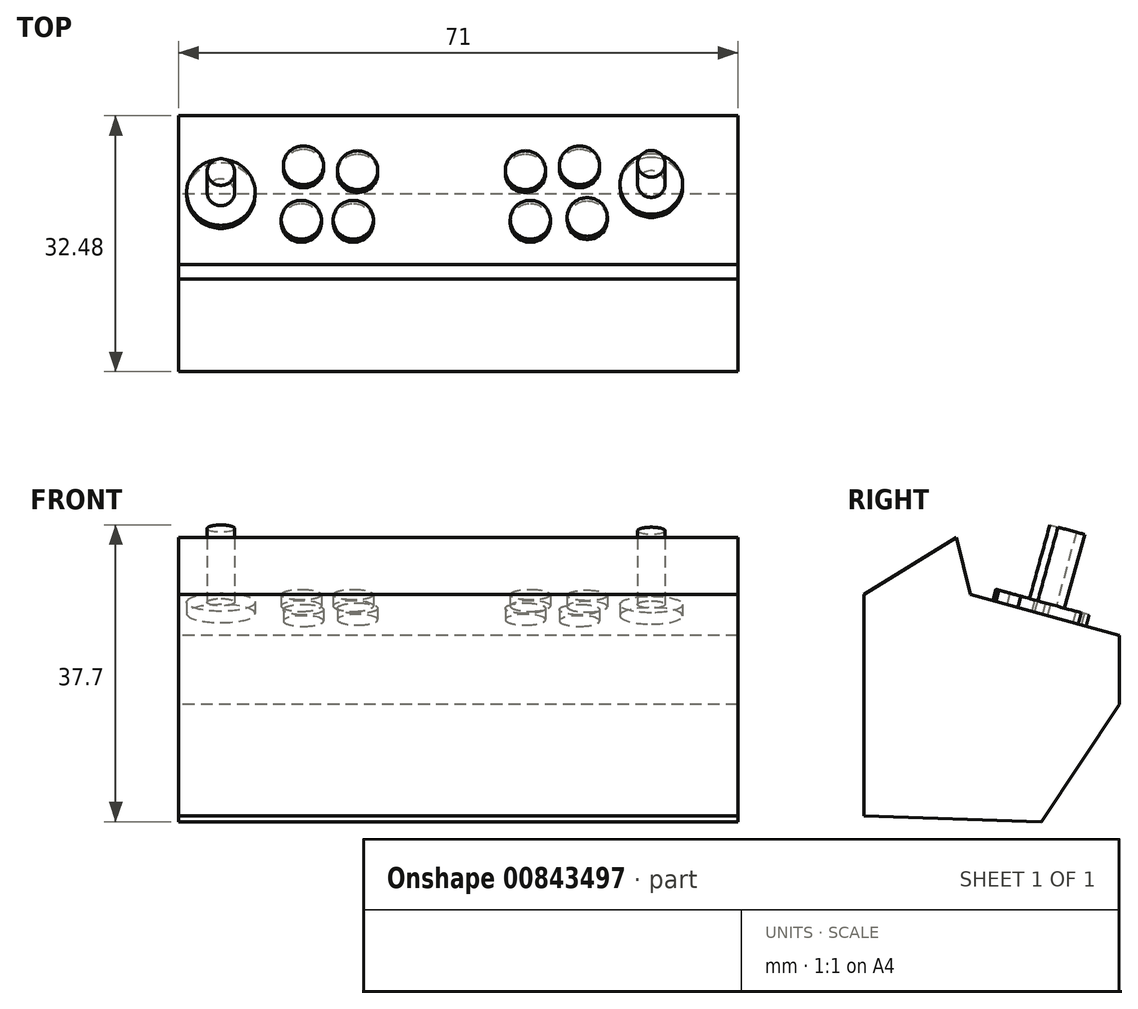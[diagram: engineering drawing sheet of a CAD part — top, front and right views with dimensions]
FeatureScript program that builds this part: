
annotation { "Feature Type Name" : "Feature", "Feature Type Description" : "" }
export const myFeature = defineFeature(function(context is Context, id is Id, definition is map)
    precondition{}
    {
        {
            var Q0;
            Q0=qCreatedBy(makeId("Right.planeOp"),FACE);
            var sketch = newSketch(context, id + "F0", { "sketchPlane" : qUnion([Q0])});
            skLineSegment(sketch, "E0", {"start": v(22.55, -11.2) * mm, "end": v(32.48, 3.7) * mm});
            skLineSegment(sketch, "E1", {"start": v(32.48, 3.7) * mm, "end": v(32.48, 12.46) * mm});
            skLineSegment(sketch, "E2", {"start": v(32.48, 12.46) * mm, "end": v(13.56, 17.66) * mm});
            skLineSegment(sketch, "E3", {"start": v(13.56, 17.66) * mm, "end": v(11.76, 24.88) * mm});
            skLineSegment(sketch, "E4", {"start": v(11.76, 24.88) * mm, "end": v(0, 17.66) * mm});
            skLineSegment(sketch, "E5", {"start": v(0, 17.66) * mm, "end": v(0, -10.48) * mm});
            skLineSegment(sketch, "E6", {"start": v(0, -10.48) * mm, "end": v(22.55, -11.2) * mm});
            skPoint(sketch, "E7.orphan", {"position": v(-45.1, 64.5) * mm});
            skPoint(sketch, "E8.start.orphan", {"position": v(-45.1, 37.53) * mm});
            skSolve(sketch);
        }
        {
            var Q0;
            Q0=makeQuery(id+"F0.imprint","IMPRINT",FACE,{"disambiguationData":[TD([[makeQuery(id+"F0.imprint","IMPRINT",EDGE,{"derivedFrom":sQuery(id+"F0.wireOp",EDGE,"E0")}),1.0]])]});
            extrude(context, id + "F1", {"entities" : qUnion([Q0]), "depth" : 65 * mm, "offsetDistance" : 25 * mm});
        }
        {
            var Q0;
            Q0=makeQuery(id+"F1.opExtrude","SWEPT_EDGE",EDGE,{"disambiguationData":[OSD([sQuery(id+"F0.wireOp",EDGE,"E0"),sQuery(id+"F0.wireOp",EDGE,"E1")])]});
            var Q1;
            Q1=makeQuery(id+"F1.opExtrude","SWEPT_EDGE",EDGE,{"disambiguationData":[OSD([sQuery(id+"F0.wireOp",EDGE,"E1"),sQuery(id+"F0.wireOp",EDGE,"E2")])]});
            fillet(context, id + "F2", {"entities" : qUnion([Q0, Q1]), "radius" : 2 * mm, "tangentPropagation" : true, "allowEdgeOverflow" : false});
        }
        {
            var Q0;
            Q0=makeQuery(id+"F1.opExtrude","SWEPT_FACE",FACE,{"disambiguationData":[OSD([sQuery(id+"F0.wireOp",EDGE,"E2")])]});
            var sketch = newSketch(context, id + "F3", { "sketchPlane" : qUnion([Q0])});
            skCircle(sketch, "E9", {"center": v(60.03, 18.6) * mm, "radius": 3.97 * mm});
            skCircle(sketch, "E10", {"center": v(5.35, 17.52) * mm, "radius": 4.35 * mm});
            skCircle(sketch, "E11", {"center": v(51.88, 14.27) * mm, "radius": 2.55 * mm});
            skCircle(sketch, "E12", {"center": v(50.9, 21.07) * mm, "radius": 2.55 * mm});
            skCircle(sketch, "E13", {"center": v(44.65, 13.9) * mm, "radius": 2.55 * mm});
            skCircle(sketch, "E14", {"center": v(44.02, 20.44) * mm, "radius": 2.55 * mm});
            skCircle(sketch, "E15", {"center": v(22.17, 13.9) * mm, "radius": 2.55 * mm});
            skCircle(sketch, "E16", {"center": v(15.56, 13.9) * mm, "radius": 2.55 * mm});
            skCircle(sketch, "E17", {"center": v(22.72, 20.44) * mm, "radius": 2.55 * mm});
            skCircle(sketch, "E18", {"center": v(15.83, 21.07) * mm, "radius": 2.55 * mm});
            skSolve(sketch);
        }
        {
            var Q0;
            Q0=makeQuery(id+"F3.imprint","IMPRINT",FACE,{"disambiguationData":[TD([[makeQuery(id+"F3.imprint","IMPRINT",EDGE,{"derivedFrom":sQuery(id+"F3.wireOp",EDGE,"E12")}),1.0]])]});
            var Q1;
            Q1=makeQuery(id+"F3.imprint","IMPRINT",FACE,{"disambiguationData":[TD([[makeQuery(id+"F3.imprint","IMPRINT",EDGE,{"derivedFrom":sQuery(id+"F3.wireOp",EDGE,"E14")}),1.0]])]});
            var Q2;
            Q2=makeQuery(id+"F3.imprint","IMPRINT",FACE,{"disambiguationData":[TD([[makeQuery(id+"F3.imprint","IMPRINT",EDGE,{"derivedFrom":sQuery(id+"F3.wireOp",EDGE,"E13")}),1.0]])]});
            var Q3;
            Q3=makeQuery(id+"F3.imprint","IMPRINT",FACE,{"disambiguationData":[TD([[makeQuery(id+"F3.imprint","IMPRINT",EDGE,{"derivedFrom":sQuery(id+"F3.wireOp",EDGE,"E11")}),1.0]])]});
            var Q4;
            Q4=makeQuery(id+"F3.imprint","IMPRINT",FACE,{"disambiguationData":[TD([[makeQuery(id+"F3.imprint","IMPRINT",EDGE,{"derivedFrom":sQuery(id+"F3.wireOp",EDGE,"E15")}),1.0]])]});
            var Q5;
            Q5=makeQuery(id+"F3.imprint","IMPRINT",FACE,{"disambiguationData":[TD([[makeQuery(id+"F3.imprint","IMPRINT",EDGE,{"derivedFrom":sQuery(id+"F3.wireOp",EDGE,"E16")}),1.0]])]});
            var Q6;
            Q6=makeQuery(id+"F3.imprint","IMPRINT",FACE,{"disambiguationData":[TD([[makeQuery(id+"F3.imprint","IMPRINT",EDGE,{"derivedFrom":sQuery(id+"F3.wireOp",EDGE,"E18")}),1.0]])]});
            var Q7;
            Q7=makeQuery(id+"F3.imprint","IMPRINT",FACE,{"disambiguationData":[TD([[makeQuery(id+"F3.imprint","IMPRINT",EDGE,{"derivedFrom":sQuery(id+"F3.wireOp",EDGE,"E17")}),1.0]])]});
            var Q8;
            Q8=makeQuery(id+"F3.imprint","IMPRINT",FACE,{"disambiguationData":[TD([[makeQuery(id+"F3.imprint","IMPRINT",EDGE,{"derivedFrom":sQuery(id+"F3.wireOp",EDGE,"E10")}),1.0]])]});
            var Q9;
            Q9=makeQuery(id+"F3.imprint","IMPRINT",FACE,{"disambiguationData":[TD([[makeQuery(id+"F3.imprint","IMPRINT",EDGE,{"derivedFrom":sQuery(id+"F3.wireOp",EDGE,"E9")}),1.0]])]});
            extrude(context, id + "F4", {"entities" : qUnion([Q0, Q1, Q2, Q3, Q4, Q5, Q6, Q7, Q8, Q9]), "operationType" : NewBodyOperationType.ADD, "depth" : 1.5 * mm, "offsetDistance" : 25 * mm});
        }
        {
            var Q0;
            Q0=makeQuery(id+"F1.opExtrude","SWEPT_FACE",FACE,{"disambiguationData":[OSD([sQuery(id+"F0.wireOp",EDGE,"E2")])]});
            var sketch = newSketch(context, id + "F5", { "sketchPlane" : qUnion([Q0])});
            skCircle(sketch, "E19", {"center": v(60.03, 18.6) * mm, "radius": 1.75 * mm});
            skCircle(sketch, "E20", {"center": v(5.35, 17.52) * mm, "radius": 1.75 * mm});
            skSolve(sketch);
        }
        {
            var Q0;
            Q0 = qSketchRegion(id + "F5", true);
            extrude(context, id + "F6", {"entities" : qUnion([Q0]), "operationType" : NewBodyOperationType.ADD, "depth" : 11.2 * mm, "offsetDistance" : 25 * mm});
        }
        {
            var Q0;
            Q0 = qSketchRegion(id + "F0", true);
            extrude(context, id + "F7", {"entities" : qUnion([Q0]), "operationType" : NewBodyOperationType.ADD, "depth" : 71 * mm, "offsetDistance" : 25 * mm});
        }
    });
